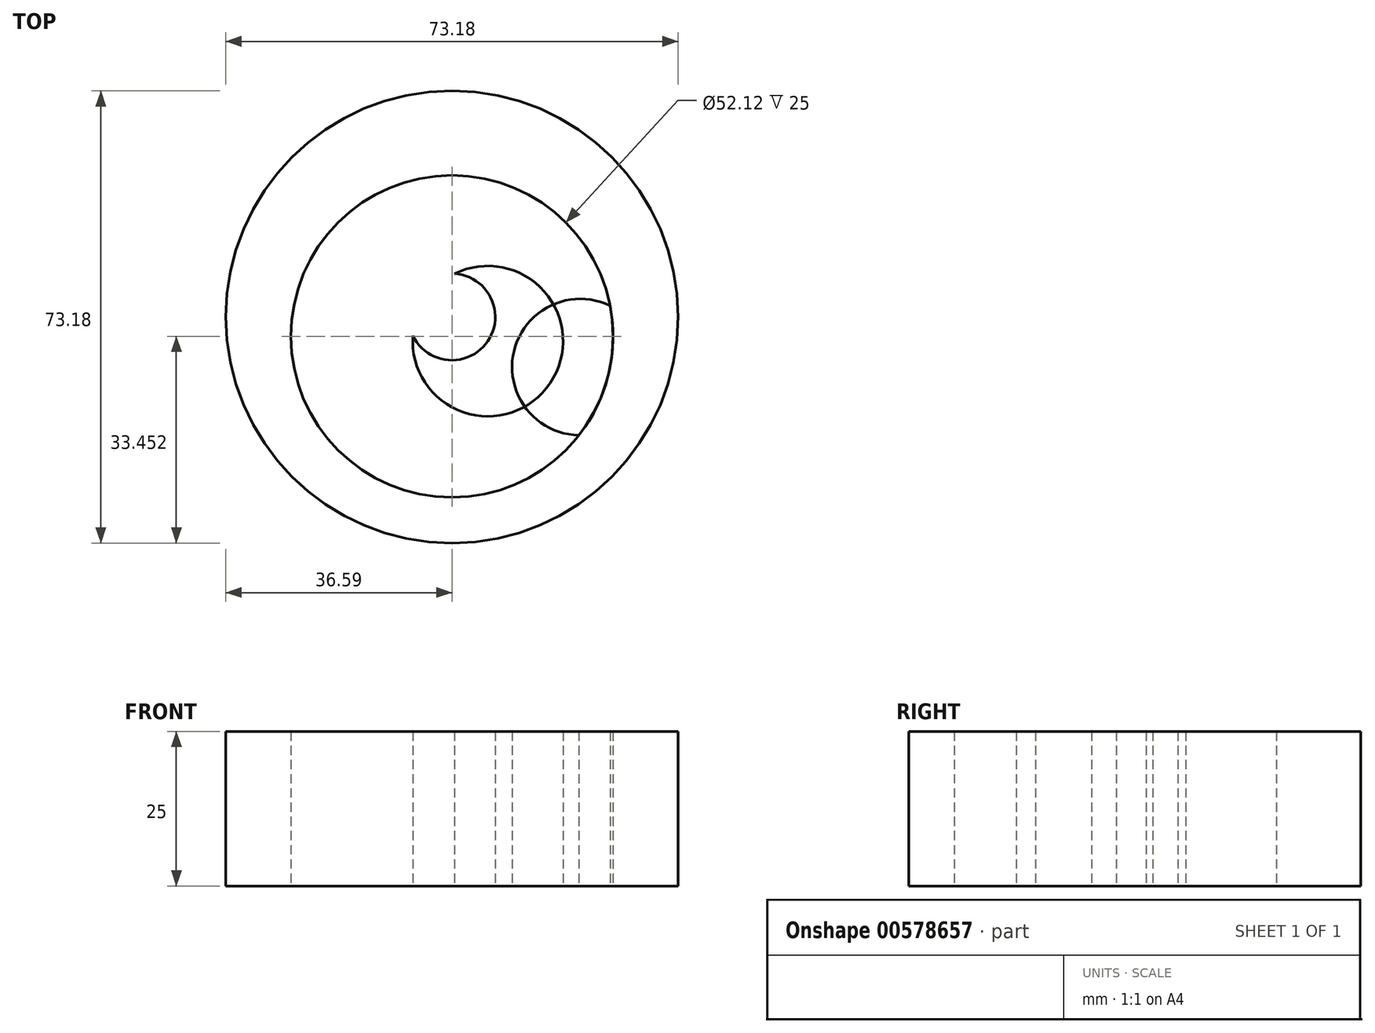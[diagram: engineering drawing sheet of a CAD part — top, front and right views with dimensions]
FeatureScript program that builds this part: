
annotation { "Feature Type Name" : "Feature", "Feature Type Description" : "" }
export const myFeature = defineFeature(function(context is Context, id is Id, definition is map)
    precondition{}
    {
        {
            var Q0;
            Q0=qCreatedBy(makeId("Top.planeOp"),FACE);
            var sketch = newSketch(context, id + "F0", { "sketchPlane" : qUnion([Q0])});
            skCircle(sketch, "E0", {"center": v(0, 0) * mm, "radius": 36.59 * mm});
            skCircle(sketch, "E1", {"center": v(0, -3.14) * mm, "radius": 26.06 * mm});
            skCircle(sketch, "E2", {"center": v(0, 0) * mm, "radius": 7 * mm});
            skCircle(sketch, "E3", {"center": v(5.81, -3.91) * mm, "radius": 12.17 * mm});
            skSolve(sketch);
        }
        {
            var Q0;
            Q0=makeQuery(id+"F0.imprint","IMPRINT",FACE,{"disambiguationData":[TD([[makeQuery(id+"F0.imprint","IMPRINT",EDGE,{"derivedFrom":sQuery(id+"F0.wireOp",EDGE,"E0")}),1.0]])]});
            var sketch = newSketch(context, id + "F1", { "sketchPlane" : qUnion([Q0])});
            skCircle(sketch, "E4", {"center": v(20.77, -8.12) * mm, "radius": 11.04 * mm});
            skSolve(sketch);
        }
        {
            var Q0;
            Q0=makeQuery(id+"F0.imprint","IMPRINT",FACE,{"disambiguationData":[TD([[makeQuery(id+"F0.imprint","IMPRINT",EDGE,{"derivedFrom":sQuery(id+"F0.wireOp",EDGE,"E0")}),1.0]])]});
            var Q1;
            {var subQ0=sQuery(id+"F0.wireOp",EDGE,"E3");var subQ1=sQuery(id+"F0.wireOp",EDGE,"E2");var subQ2=makeQuery(id+"F0.imprint","INTERSECT",VERTEX,{"disambiguationData":[OD(0.0)],"derivedFrom":[subQ1,subQ0]});Q1=makeQuery(id+"F0.imprint","IMPRINT",FACE,{"disambiguationData":[TD([[makeQuery(id+"F0.imprint","IMPRINT",EDGE,{"disambiguationData":[TD([[subQ2,-1.0]])],"derivedFrom":subQ1}),-1.0]])]});}
            var Q2;
            {var subQ0=sQuery(id+"F1.wireOp",EDGE,"E4");var subQ1=makeQuery(id+"F0.imprint","IMPRINT",EDGE,{"derivedFrom":sQuery(id+"F0.wireOp",EDGE,"E1")});var subQ2=makeQuery(id+"F1.imprint","INTERSECT",VERTEX,{"disambiguationData":[OD(0.0)],"derivedFrom":[subQ1,subQ0]});Q2=makeQuery(id+"F1.imprint","IMPRINT",FACE,{"disambiguationData":[TD([[makeQuery(id+"F1.imprint","IMPRINT",EDGE,{"disambiguationData":[TD([[subQ2,1.0]])],"derivedFrom":subQ0}),1.0]])]});}
            extrude(context, id + "F2", {"entities" : qUnion([Q0, Q1, Q2]), "depth" : 25 * mm, "offsetDistance" : 25 * mm});
        }
    });
